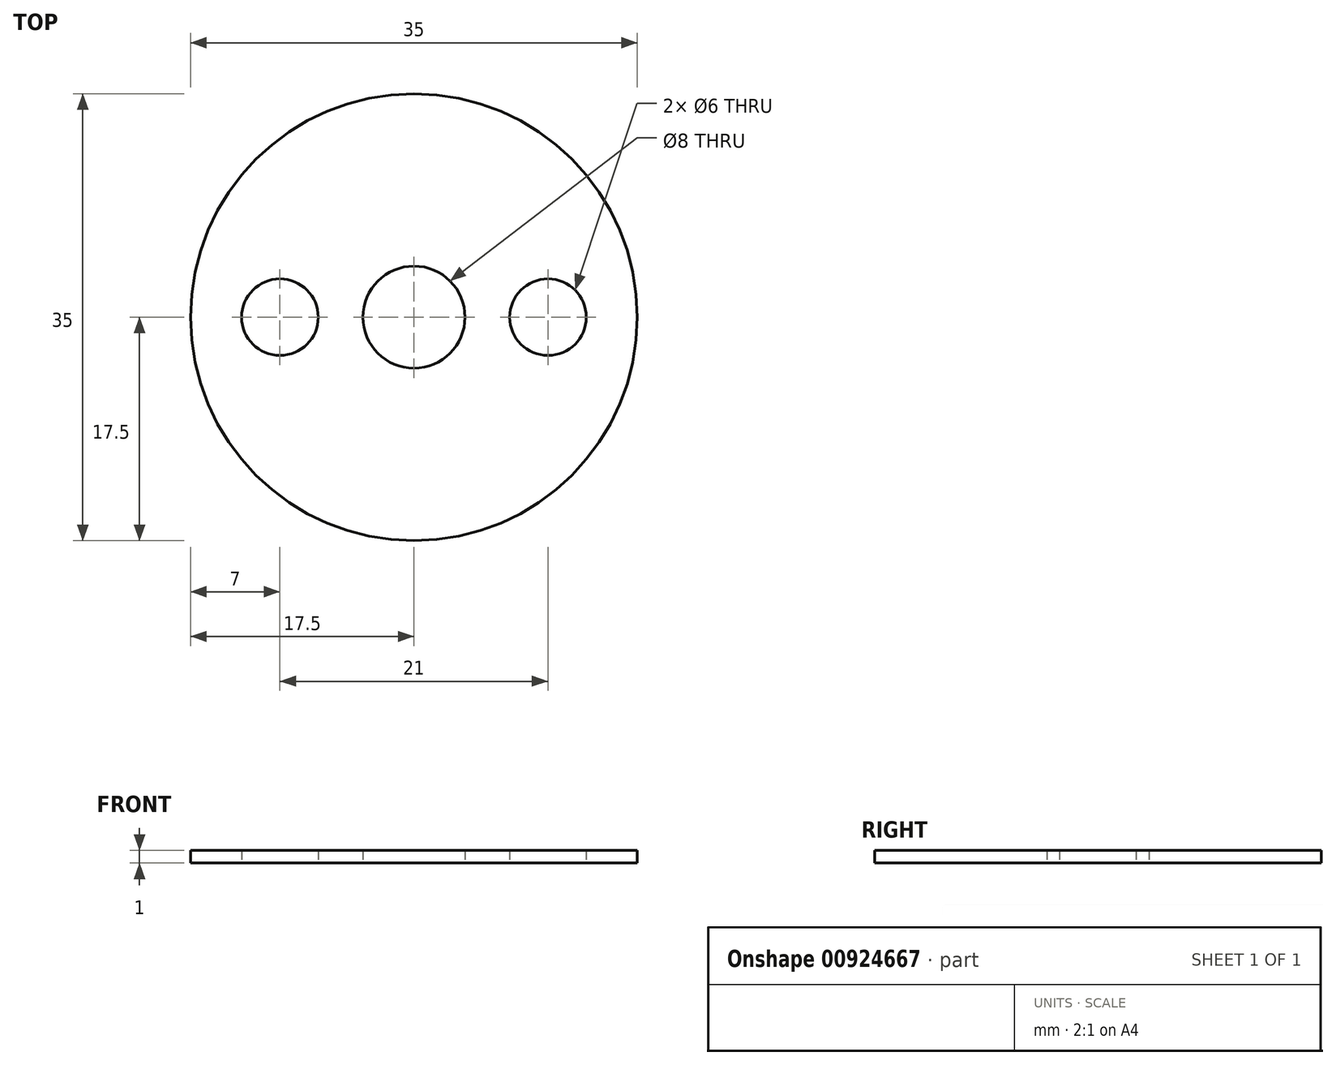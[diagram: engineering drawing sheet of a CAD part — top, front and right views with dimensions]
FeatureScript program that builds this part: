
annotation { "Feature Type Name" : "Feature", "Feature Type Description" : "" }
export const myFeature = defineFeature(function(context is Context, id is Id, definition is map)
    precondition{}
    {
        {
            var Q0;
            Q0=qCreatedBy(makeId("Top.planeOp"),FACE);
            var sketch = newSketch(context, id + "F0", { "sketchPlane" : qUnion([Q0])});
            skCircle(sketch, "E0", {"center": v(0, 0) * mm, "radius": 17.5 * mm});
            skCircle(sketch, "E1", {"center": v(-10.5, 0) * mm, "radius": 3 * mm});
            skCircle(sketch, "E2", {"center": v(10.5, 0) * mm, "radius": 3 * mm});
            skCircle(sketch, "E3", {"center": v(0, 0) * mm, "radius": 4 * mm});
            skSolve(sketch);
        }
        {
            var Q0;
            Q0=makeQuery(id+"F0.imprint","IMPRINT",FACE,{"disambiguationData":[TD([[makeQuery(id+"F0.imprint","IMPRINT",EDGE,{"derivedFrom":sQuery(id+"F0.wireOp",EDGE,"E0")}),1.0]])]});
            extrude(context, id + "F1", {"entities" : qUnion([Q0]), "depth" : 1 * mm, "offsetDistance" : 25 * mm});
        }
    });
